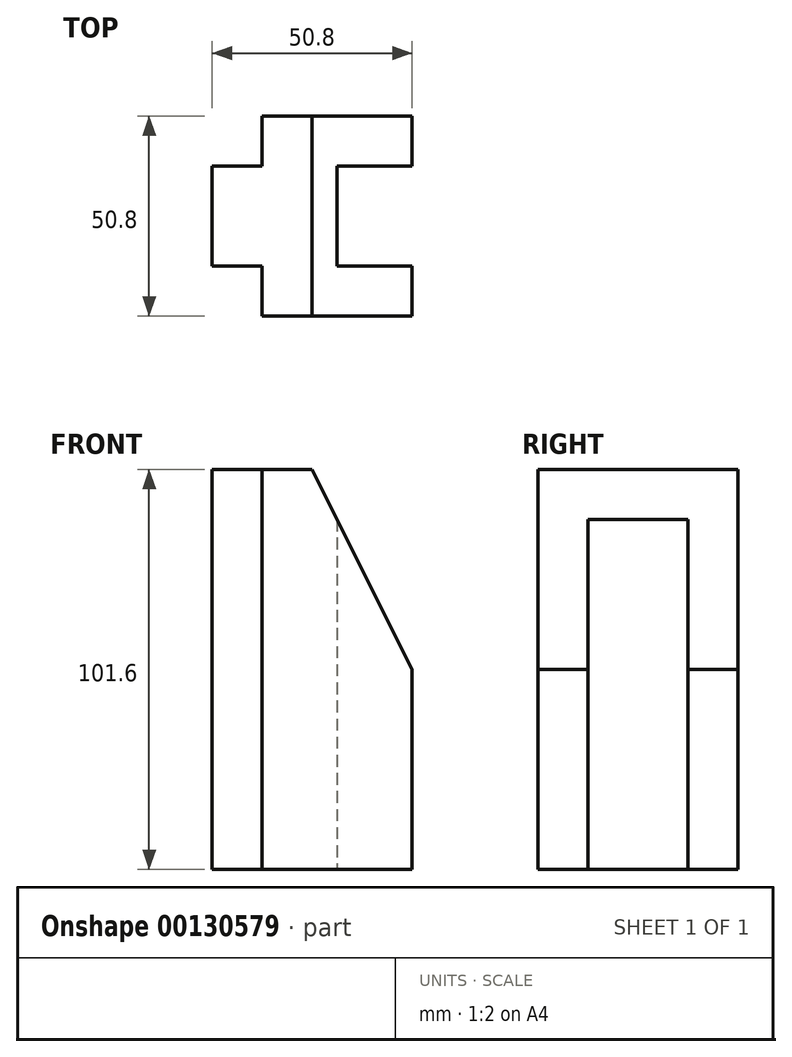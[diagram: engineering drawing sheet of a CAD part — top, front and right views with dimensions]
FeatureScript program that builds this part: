
annotation { "Feature Type Name" : "Feature", "Feature Type Description" : "" }
export const myFeature = defineFeature(function(context is Context, id is Id, definition is map)
    precondition{}
    {
        {
            var Q0;
            Q0=qCreatedBy(makeId("Top.planeOp"),FACE);
            var sketch = newSketch(context, id + "F0", { "sketchPlane" : qUnion([Q0])});
            skLineSegment(sketch, "E0", {"start": v(0, 0) * mm, "end": v(-12.7, 0) * mm});
            skLineSegment(sketch, "E1", {"start": v(-12.7, 0) * mm, "end": v(-12.7, 12.7) * mm});
            skLineSegment(sketch, "E2", {"start": v(-12.7, 12.7) * mm, "end": v(-25.4, 12.7) * mm});
            skLineSegment(sketch, "E3", {"start": v(-25.4, 12.7) * mm, "end": v(-25.4, 38.1) * mm});
            skLineSegment(sketch, "E4", {"start": v(-25.4, 38.1) * mm, "end": v(-12.7, 38.1) * mm});
            skLineSegment(sketch, "E5", {"start": v(-12.7, 38.1) * mm, "end": v(-12.7, 50.8) * mm});
            skLineSegment(sketch, "E6", {"start": v(-12.7, 50.8) * mm, "end": v(25.4, 50.8) * mm});
            skLineSegment(sketch, "E7", {"start": v(25.4, 50.8) * mm, "end": v(25.4, 38.1) * mm});
            skLineSegment(sketch, "E8", {"start": v(25.4, 38.1) * mm, "end": v(6.35, 38.1) * mm});
            skLineSegment(sketch, "E9", {"start": v(6.35, 38.1) * mm, "end": v(6.35, 12.7) * mm});
            skLineSegment(sketch, "E10", {"start": v(6.35, 12.7) * mm, "end": v(25.4, 12.7) * mm});
            skLineSegment(sketch, "E11", {"start": v(25.4, 12.7) * mm, "end": v(25.4, 0) * mm});
            skLineSegment(sketch, "E12", {"start": v(25.4, 0) * mm, "end": v(0, 0) * mm});
            skLineSegment(sketch, "E13", {"start": v(0, 50.8) * mm, "end": v(0, 0) * mm});
            skSolve(sketch);
        }
        {
            var Q0;
            Q0=makeQuery(id+"F0.imprint","IMPRINT",FACE,{"disambiguationData":[TD([[makeQuery(id+"F0.imprint","IMPRINT",EDGE,{"derivedFrom":sQuery(id+"F0.wireOp",EDGE,"E0")}),-1.0]])]});
            var Q1;
            {var subQ0=sQuery(id+"F0.wireOp",EDGE,"E7");Q1=makeQuery(id+"F0.imprint","IMPRINT",FACE,{"disambiguationData":[TD([[makeQuery(id+"F0.imprint","IMPRINT",EDGE,{"derivedFrom":subQ0}),-1.0]])]});}
            extrude(context, id + "F1", {"entities" : qUnion([Q0, Q1]), "depth" : 101.6 * mm});
        }
        {
            var Q0;
            Q0=makeQuery(id+"F1.opExtrude","SWEPT_FACE",FACE,{"disambiguationData":[OSD([sQuery(id+"F0.wireOp",EDGE,"E0"),sQuery(id+"F0.wireOp",EDGE,"E12")])]});
            var sketch = newSketch(context, id + "F2", { "sketchPlane" : qUnion([Q0])});
            skLineSegment(sketch, "E14", {"start": v(0, 101.6) * mm, "end": v(25.4, 50.8) * mm});
            skSolve(sketch);
        }
        {
            var Q0;
            Q0 = qSketchRegion(id + "F2", true);
            var Q1;
            {var subQ0=sQuery(id+"F2.wireOp",EDGE,"E14");Q1=makeQuery(id+"F2.imprint","IMPRINT",FACE,{"disambiguationData":[TD([[makeQuery(id+"F2.imprint","IMPRINT",EDGE,{"derivedFrom":subQ0}),1.0]])]});}
            extrude(context, id + "F3", {"entities" : qUnion([Q0, Q1]), "operationType" : NewBodyOperationType.REMOVE, "endBound" : BoundingType.THROUGH_ALL, "oppositeDirection" : true, "depth" : 25.4 * mm});
        }
    });
